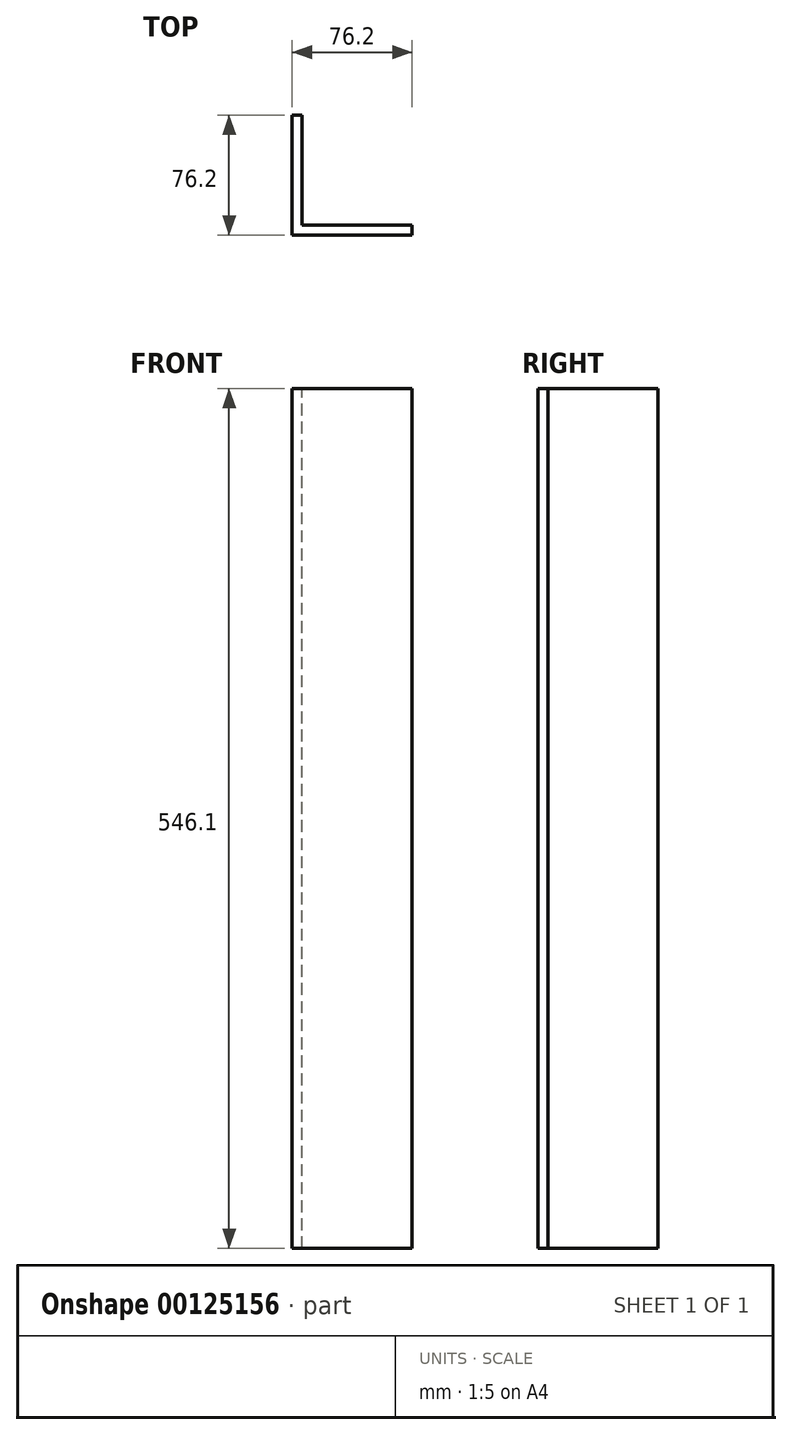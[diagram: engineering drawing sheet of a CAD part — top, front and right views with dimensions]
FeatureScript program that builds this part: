
annotation { "Feature Type Name" : "Feature", "Feature Type Description" : "" }
export const myFeature = defineFeature(function(context is Context, id is Id, definition is map)
    precondition{}
    {
        {
            var Q0;
            Q0=qCreatedBy(makeId("Top.planeOp"),FACE);
            var sketch = newSketch(context, id + "F0", { "sketchPlane" : qUnion([Q0])});
            skLineSegment(sketch, "E0", {"start": v(0, 76.2) * mm, "end": v(0, 0) * mm});
            skLineSegment(sketch, "E1", {"start": v(0, 0) * mm, "end": v(76.2, 0) * mm});
            skLineSegment(sketch, "E2.0", {"start": v(6.35, 6.35) * mm, "end": v(76.2, 6.35) * mm});
            skLineSegment(sketch, "E2.1", {"start": v(6.35, 76.2) * mm, "end": v(6.35, 6.35) * mm});
            skLineSegment(sketch, "E3", {"start": v(0, 76.2) * mm, "end": v(6.35, 76.2) * mm});
            skLineSegment(sketch, "E4", {"start": v(76.2, 6.35) * mm, "end": v(76.2, 0) * mm});
            skSolve(sketch);
        }
        {
            var Q0;
            Q0=qSketchRegion(id+"F0",true);
            extrude(context, id + "F1", {"entities" : qUnion([Q0]), "oppositeDirection" : true, "depth" : 546.1 * mm});
        }
    });
